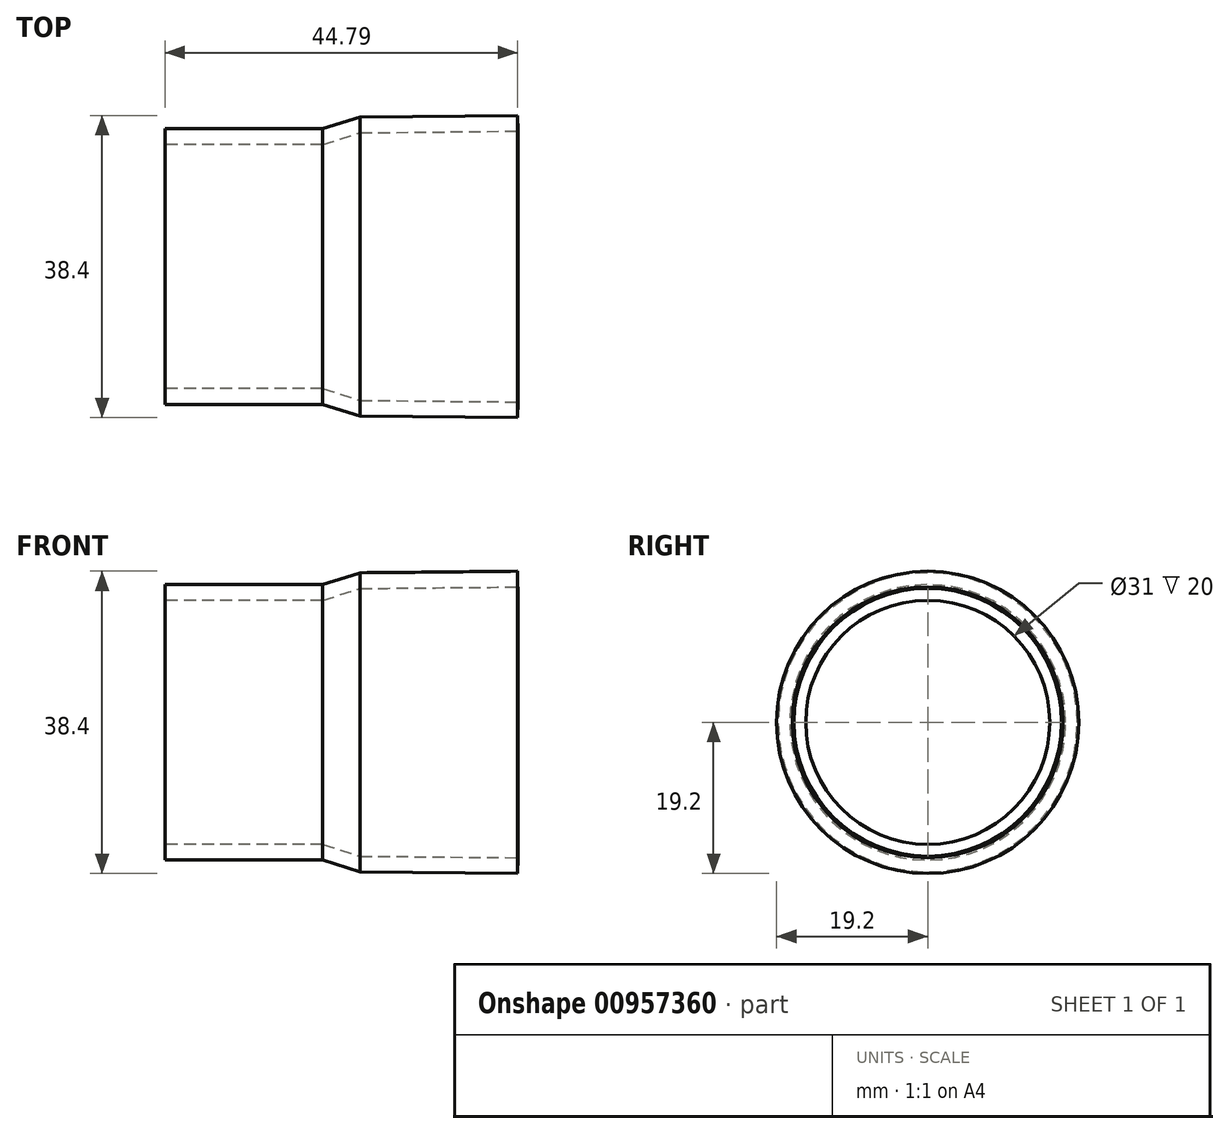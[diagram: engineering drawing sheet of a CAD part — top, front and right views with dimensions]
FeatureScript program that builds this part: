
annotation { "Feature Type Name" : "Feature", "Feature Type Description" : "" }
export const myFeature = defineFeature(function(context is Context, id is Id, definition is map)
    precondition{}
    {
        {
            var Q0;
            Q0=qCreatedBy(makeId("Top.planeOp"),FACE);
            var sketch = newSketch(context, id + "F0", { "sketchPlane" : qUnion([Q0])});
            skLineSegment(sketch, "E0", {"start": v(20.92, 17) * mm, "end": v(16.15, 15.5) * mm});
            skLineSegment(sketch, "E1", {"start": v(16.15, 15.5) * mm, "end": v(-3.85, 15.5) * mm});
            skLineSegment(sketch, "E2", {"start": v(-3.85, 15.5) * mm, "end": v(-3.85, 17.5) * mm});
            skLineSegment(sketch, "E3", {"start": v(-3.85, 17.5) * mm, "end": v(16.15, 17.5) * mm});
            skLineSegment(sketch, "E4", {"start": v(16.15, 17.5) * mm, "end": v(20.92, 19) * mm});
            skLineSegment(sketch, "E5", {"start": v(-43.34, 0) * mm, "end": v(39.1, 0) * mm, "construction": true});
            skPoint(sketch, "E6", {"position": v(7.34, 15.5) * mm});
            skLineSegment(sketch, "E7", {"start": v(7.34, 15.5) * mm, "end": v(7.34, 0) * mm, "construction": true});
            skLineSegment(sketch, "E8", {"start": v(20.92, 19) * mm, "end": v(40.92, 19.2) * mm});
            skLineSegment(sketch, "E9", {"start": v(40.92, 19.2) * mm, "end": v(40.94, 17.2) * mm});
            skLineSegment(sketch, "E10", {"start": v(40.94, 17.2) * mm, "end": v(20.92, 17) * mm});
            skPoint(sketch, "E11", {"position": v(40.94, 17.2) * mm});
            skPoint(sketch, "E12", {"position": v(30.93, 17.1) * mm});
            skPoint(sketch, "E13", {"position": v(20.92, 17) * mm});
            skLineSegment(sketch, "E14", {"start": v(40.94, 17.2) * mm, "end": v(40.94, 0) * mm, "construction": true});
            skLineSegment(sketch, "E15", {"start": v(20.92, 17) * mm, "end": v(20.92, 0) * mm, "construction": true});
            skLineSegment(sketch, "E16", {"start": v(20.92, 19) * mm, "end": v(20.92, 17) * mm, "construction": true});
            skSolve(sketch);
        }
        {
            var Q0;
            Q0=makeQuery(id+"F0.imprint","IMPRINT",FACE,{"disambiguationData":[TD([[makeQuery(id+"F0.imprint","IMPRINT",EDGE,{"derivedFrom":sQuery(id+"F0.wireOp",EDGE,"E0")}),-1.0]])]});
            var Q1;
            Q1=sQuery(id+"F0.wireOp",EDGE,"E5");
            revolve(context, id + "F1", {"surfaceOperationType" : NewSurfaceOperationType.NEW, "entities" : qUnion([Q0]), "axis" : qUnion([Q1]), "revolveType" : RevolveType.FULL});
        }
    });
